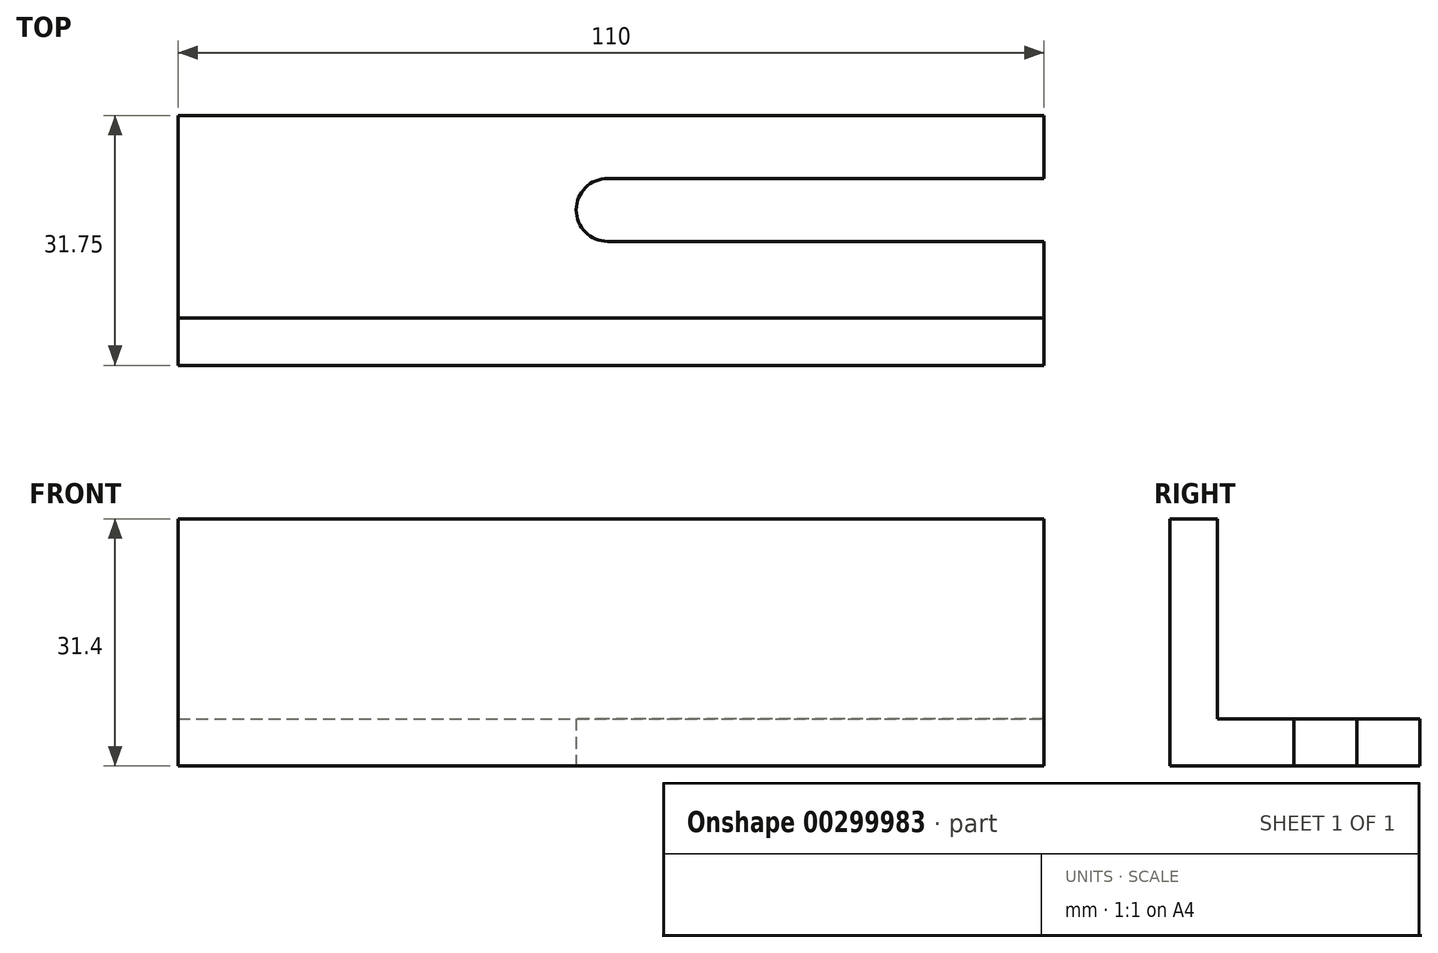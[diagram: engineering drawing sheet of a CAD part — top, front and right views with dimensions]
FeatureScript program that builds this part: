
annotation { "Feature Type Name" : "Feature", "Feature Type Description" : "" }
export const myFeature = defineFeature(function(context is Context, id is Id, definition is map)
    precondition{}
    {
        {
            var Q0;
            Q0=qCreatedBy(makeId("Top.planeOp"),FACE);
            var sketch = newSketch(context, id + "F0", { "sketchPlane" : qUnion([Q0])});
            skLineSegment(sketch, "E0.bottom", {"start": v(0, 0) * mm, "end": v(110, 0) * mm});
            skLineSegment(sketch, "E0.top", {"start": v(0, 31.75) * mm, "end": v(110, 31.75) * mm});
            skLineSegment(sketch, "E0.left", {"start": v(0, 0) * mm, "end": v(0, 31.75) * mm});
            skLineSegment(sketch, "E0.right", {"start": v(110, 0) * mm, "end": v(110, 31.75) * mm});
            skSolve(sketch);
        }
        {
            var Q0;
            Q0=qSketchRegion(id+"F0",true);
            extrude(context, id + "F1", {"entities" : qUnion([Q0]), "depth" : 6 * mm, "offsetDistance" : 25 * mm});
        }
        {
            var Q0;
            Q0=makeQuery(id+"F1.opExtrude","CAP_FACE",FACE,{"disambiguationData":[OSD([sQuery(id+"F0.wireOp",EDGE,"E0.bottom"),sQuery(id+"F0.wireOp",EDGE,"E0.top"),sQuery(id+"F0.wireOp",EDGE,"E0.left"),sQuery(id+"F0.wireOp",EDGE,"E0.right")])],"isStart":false});
            var sketch = newSketch(context, id + "F2", { "sketchPlane" : qUnion([Q0])});
            skLineSegment(sketch, "E1.bottom", {"start": v(0, 0) * mm, "end": v(110, 0) * mm});
            skLineSegment(sketch, "E1.top", {"start": v(0, 6) * mm, "end": v(110, 6) * mm});
            skLineSegment(sketch, "E1.left", {"start": v(0, 0) * mm, "end": v(0, 6) * mm});
            skLineSegment(sketch, "E1.right", {"start": v(110, 0) * mm, "end": v(110, 6) * mm});
            skSolve(sketch);
        }
        {
            var Q0;
            Q0=qSketchRegion(id+"F2",true);
            extrude(context, id + "F3", {"entities" : qUnion([Q0]), "operationType" : NewBodyOperationType.ADD, "depth" : 25.4 * mm, "offsetDistance" : 25 * mm});
        }
        {
            var Q0;
            Q0=makeQuery(id+"F1.opExtrude","CAP_FACE",FACE,{"disambiguationData":[OSD([sQuery(id+"F0.wireOp",EDGE,"E0.bottom"),sQuery(id+"F0.wireOp",EDGE,"E0.top"),sQuery(id+"F0.wireOp",EDGE,"E0.left"),sQuery(id+"F0.wireOp",EDGE,"E0.right")])],"isStart":true});
            var sketch = newSketch(context, id + "F4", { "sketchPlane" : qUnion([Q0])});
            skCircle(sketch, "E2", {"center": v(54.56, -19.75) * mm, "radius": 4 * mm});
            skLineSegment(sketch, "E3", {"start": v(54.56, -19.75) * mm, "end": v(54.56, -15.75) * mm});
            skLineSegment(sketch, "E4", {"start": v(54.56, -15.75) * mm, "end": v(110, -15.75) * mm});
            skLineSegment(sketch, "E5", {"start": v(54.56, -19.75) * mm, "end": v(54.56, -23.75) * mm});
            skLineSegment(sketch, "E6", {"start": v(54.56, -23.75) * mm, "end": v(110, -23.75) * mm});
            skLineSegment(sketch, "E7", {"start": v(110, -23.75) * mm, "end": v(110, -15.75) * mm});
            skSolve(sketch);
        }
        {
            var Q0;
            Q0=qSketchRegion(id+"F4",true);
            extrude(context, id + "F5", {"entities" : qUnion([Q0]), "operationType" : NewBodyOperationType.REMOVE, "endBound" : BoundingType.THROUGH_ALL, "oppositeDirection" : true, "depth" : 25 * mm, "offsetDistance" : 25 * mm});
        }
    });
